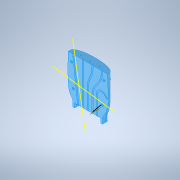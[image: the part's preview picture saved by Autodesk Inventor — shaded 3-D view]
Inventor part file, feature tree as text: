
AUTODESK INVENTOR PART (.ipt)
format: ipt  version: 2021 (Build 250183000, 183)  size: 1,971,200 bytes
history: native  units: mm
features: sketch x38, extrude x24, other x21, fillet x19, plane x11, sweep x4, hole x4, delete_face x1, mirror x1
ambient origin geometry x8: Origin, YZ Plane, XZ Plane, XY Plane, X Axis, Y Axis, Z Axis, Center Point
bodies: Volumenkörper2 (feature_tree), Volumenkörper3 (feature_tree), Volumenkörper4 (feature_tree), Volumenkörper8 (feature_tree), Volumenkörper9 (feature_tree), Volumenkörper10 (feature_tree), Volumenkörper11 (feature_tree), Volumenkörper15 (feature_tree), Volumenkörper16 (feature_tree), Volumenkörper17 (feature_tree), Volumenkörper18 (feature_tree), Volumenkörper19 (feature_tree), Volumenkörper20 (feature_tree), Volumenkörper21 (feature_tree), Volumenkörper24 (feature_tree), Volumenkörper1 (feature_tree)
feature tree (123):
  other  "Form1"
  plane  "Arbeitsebene1"
  extrude  "Extrusion1"  Depth=24.0mm
  fillet  "Rundung1"  Radius=68.0mm
  other  "Kombinieren1"
  fillet  "Rundung2"  Radius=34.0mm
  plane  "Arbeitsebene2"
  extrude  "Extrusion2"  Depth=30.0mm TaperAngle=0.0deg
  other  "Kombinieren2"
  extrude  "Extrusion3"  Depth=15.0mm
  other  "Kombinieren3"
  extrude  "Extrusion4"  Depth=12.0mm
  extrude  "Extrusion10"  Depth=12.0mm
  other  "Kombinieren6"
  plane  "Arbeitsebene3"
  extrude  "Extrusion11"  Depth=9.6mm
  other  "Kombinieren7"
  fillet  "Rundung4"  Radius=9.6mm
  sketch  "Skizze12"  dims[d23=30.0mm d24=45.0mm]
  plane  "Arbeitsebene5"
  extrude  "Daumen Fingerverbindung alt"  Depth=45.0mm
  extrude  "Extrusion30"  Depth=88.7mm TaperAngle=0.0deg
  sketch  "Skizze52"  dims[d209=54.0mm]
  extrude  "Extrusion31"  Depth=30.0mm
  extrude  "Extrusion32"  Depth=60.0mm
  extrude  "Extrusion15"  Depth=2.0mm
  fillet  "Rundung6"  Radius=3.0mm
  fillet  "Rundung19"  Radius=2.0mm
  fillet  "Rundung17"  Radius=7.75mm
  plane  "Arbeitsebene17"
  extrude  "Extrusion33"  Depth=2.0mm
  fillet  "Rundung18"  [1 undecoded]
  other  "Kombinieren8"
  extrude  "Extrusion16"  Depth=111.5mm TaperAngle=0.0deg
  extrude  "Extrusion17"  Depth=8.0mm
  extrude  "Extrusion18"  Depth=5.0mm
  fillet  "Rundung7"  Radius=6.981317mm
  other  "Kombinieren9"
  fillet  "Rundung8"  Radius=9.6mm
  delete_face  "Fläche löschen1"
  fillet  "Rundung10"  Radius=26.0mm
  plane  "Arbeitsebene6"
  plane  "Arbeitsebene7"
  extrude  "Extrusion19"  TaperAngle=0.0deg  [1 undecoded]
  fillet  "Rundung13"  Radius=15.0mm
  sweep  "Sweeping1"
  other  "Kombinieren10"
  fillet  "Rundung11"  Radius=16.0mm
  fillet  "Rundung12"  Radius=60.0mm
  extrude  "Extrusion20"  Depth=12.0mm
  other  "Kombinieren12"
  other  "Kombinieren13"
  plane  "Arbeitsebene11"
  extrude  "Extrusion22"  Depth=1.0mm
  mirror  "Spiegeln2"
  other  "Kombinieren14"
  extrude  "Extrusion23"  Depth=3.4mm
  fillet  "Rundung14"  Radius=30.0mm
  other  "Kombinieren15"
  fillet  "Rundung15"  Radius=5.0mm
  plane  "Arbeitsebene14"
  plane  "Arbeitsebene13"
  sweep  "Sweeping2"
  sweep  "Sweeping3"
  sweep  "Sweeping4"
  extrude  "Extrusion34"  Depth=2.5mm
  other  "Kombinieren17"
  other  "Kombinieren20"
  other  "Kombinieren18"
  other  "Kombinieren19"
  hole  "Bohrung2"  [1 undecoded]
  hole  "Bohrung3"  [1 undecoded]
  plane  "Arbeitsebene16"
  hole  "Bohrung4"  [1 undecoded]
  hole  "Bohrung5"  [1 undecoded]
  fillet  "Rundung20"  Radius=30.0mm
  extrude  "Extrusion37"  Depth=3.0mm
  extrude  "Extrusion36"  Depth=6.0mm
  fillet  "Rundung23"  Radius=10.8mm
  extrude  "Hand_Fingerverbindungen"  [1 undecoded]
  extrude  "Hand_Handhälften"  Depth=32.4mm
  other  "Fingerverbindung_kleinere_Durchmesser"
  other  "Aktivieren bei Handflächenaussenseite"
  fillet  "Rundung Hanflächenaussenseite"  Radius=2.4mm
  other  "Aktivieren bei Handflächeninnenseite"
  fillet  "Rundungi Handflächeninnenseite"  Radius=10.8mm
  sketch  "Skizze1"  dims[d0=-70.0mm d1=24.0mm d2=68.0mm d3=34.0mm]
  sketch  "Skizze2"  dims[d4=16.0mm d5=30.0mm d6=0.0mm]
  sketch  "Skizze3"  dims[d7=5.0mm d8=15.0mm]
  sketch  "Skizze4"  dims[d9=50.0mm d15=12.0mm]
  sketch  "Skizze10"  dims[d16=12.0mm d17=12.0mm]
  sketch  "Skizze11"  dims[d18=9.6mm d19=9.6mm d21=9.6mm]
  sketch  "Skizze14"  dims[d25=45.0mm d27=88.7mm d28=0.0mm]
  sketch  "Skizze17"  dims[d29=45.0mm d31=30.0mm]
  sketch  "Skizze18"  dims[d32=37.2mm d33=60.0mm]
  sketch  "Skizze19"  dims[d34=100.0mm d35=0.0mm d36=9.6mm d37=3.0mm d39=2.0mm d40=7.75mm]
  sketch  "Skizze20"  dims[d41=102.5mm d42=0.0mm d86=2.0mm d87=0.0mm]
  sketch  "Skizze22"  dims[d88=1.0mm d89=111.5mm d90=0.0mm]
  sketch  "Skizze27"  dims[d91=35.0mm d92=8.0mm]
  sketch  "Skizze28"  dims[d93=44.25mm d94=0.0mm d96=5.0mm d97=6.981317mm d99=9.6mm d102=26.0mm]
  sketch  "Skizze29"  dims[d103=90.0deg d104=0.0mm d107=15.0mm]
  sketch  "Skizze31"  dims[d108=25.0mm d109=49.25mm d110=0.0mm d123=16.0mm d124=60.0mm]
  sketch  "Skizze32"  dims[d125=30.0mm d126=12.0mm]
  sketch  "Skizze35"  dims[d127=10.0mm d128=0.0mm d129=1.0mm]
  sketch  "Skizze36"  dims[d130=5.0mm d131=3.4mm d133=30.0mm d134=0.0mm d135=5.0mm]
  sketch  "Skizze37"  dims[d136=3.4mm d138=90.0mm d139=0.0mm]
  sketch  "Skizze38"  dims[d141=17.5mm d142=15.0mm]
  sketch  "Skizze39"  dims[d143=45.0mm d144=90.0mm d145=0.0mm]
  sketch  "Skizze40"  dims[d146=5.0mm d147=2.5mm]
  sketch  "Skizze41"  dims[d149=6.0mm d150=2.0mm]
  sketch  "Skizze42"  dims[d151=6.0mm d161=30.0mm d162=3.0mm]
  sketch  "Skizze44"  dims[d163=6.0mm d164=32.4mm]
  sketch  "Skizze45"  dims[d165=37.5mm d166=0.0mm d183=0.0mm d184=0.0mm d186=30.0mm]
  sketch  "Skizze46"  dims[d187=1.0mm d188=3.0mm]
  sketch  "Skizze47"  dims[d189=3.0mm d190=6.0mm d191=10.8mm]
  sketch  "Skizze50"  dims[d192=70.0mm d193=80.0mm d194=0.0mm d195=0.0mm d204=-1.5mm]
  sketch  "Skizze51"  dims[d205=2.4mm d206=32.4mm d207=2.4mm d208=10.8mm]
  sketch  "Skizze53"  dims[d210=54.0mm]
  sketch  "Skizze54"  dims[d211=13.6mm d212=0.0mm]
  sketch  "Skizze55"  dims[d213=50.0mm]
  sketch  "Skizze57"  dims[d214=9.0mm]
  sketch  "Skizze58"  dims[d215=100.0mm d216=0.0mm d217=2.0mm d218=3.0mm d220=1.745329mm d231=6.0mm d232=92.75mm d233=0.0mm d234=35.0mm d235=116.5mm d236=0.0mm d243=10.0mm d244=3.0mm d245=0.0mm d246=0.0mm d247=21.6mm d248=0.0mm d249=21.6mm d250=0.0mm d251=10.8mm d252=3.0mm d253=0.0mm d254=0.0mm d255=0.0mm d256=0.0mm d257=32.4mm d258=10.8mm d259=30.0mm d260=35.0mm d261=20.0mm d262=35.0mm d263=3.0mm d264=10.8mm d266=0.0mm d267=0.0mm d268=0.0mm d276=0.0mm d277=21.6mm d279=0.5mm d280=3.4mm d281=6.0mm d282=6.5mm d283=4.0mm d284=90.0deg d285=6.0mm d286=0.0mm d287=0.0mm d288=21.6mm d289=0.0mm d290=21.6mm d291=2.4mm d292=6.0mm d293=6.0mm d294=2.0mm d295=90.0deg d296=8.0mm d297=0.0mm d298=0.0mm d299=0.0mm d300=0.0mm d301=0.0mm d302=0.0mm d303=0.0mm d304=0.0mm d305=0.0mm d306=-12.25mm d307=5.5mm d308=6.0mm d309=10.0mm d310=13.8mm d311=90.0deg d312=18.25mm d313=0.0mm d314=18.0mm d315=18.0mm d316=37.0mm d317=37.0mm d318=33.0mm d319=33.0mm d320=33.0mm d321=33.0mm d322=4.2mm d323=6.0mm d324=10.0mm d325=13.8mm d326=90.0deg d327=8.55mm d328=0.0mm d329=0.0mm d330=0.0mm d331=0.0mm d332=0.0mm d333=0.0mm d334=0.0mm d335=0.0mm d336=0.0mm d345=0.5mm d346=16.2mm d349=10.0mm d350=30.0mm d351=0.0mm d354=9.6mm d357=15.0mm d358=0.0mm d359=22.68928mm d360=6.0mm d361=56.3mm d362=6.0mm d363=3.0mm d364=6.0mm d365=7.75mm d366=30.0mm d367=0.0mm d369=-9.5mm d370=2.4mm d371=6.0mm d372=4.8mm d373=30.0mm d374=0.0mm d375=5.0mm d376=3.0mm d377=10.0mm d379=3.0mm d380=2.0mm d381=4.8mm d382=37.0mm d383=0.0mm d384=14.0mm d385=3.0mm d386=1.0mm d399=10.8mm d400=32.4mm d401=1.0mm d402=1.0mm d403=6.0mm d404=6.0mm d405=40.0mm d406=0.0mm d407=2.0mm d415=1.5mm d416=2.0mm d417=4.8mm d418=40.0mm d419=0.0mm d420=2.0mm d66=0.5mm d67=0.872665mm d68=0.5mm d69=0.872665mm d82=0.5mm d83=0.872665mm d84=0.5mm d85=0.872665mm d98=0.872665mm d100=0.872665mm d140=0.5mm d152=0.872665mm d153=0.872665mm d221=0.5mm d222=0.872665mm d223=0.5mm d224=0.872665mm]
  other  "Größe1"
note: 7 required parameter values undecoded (feature->parameter linkage not recoverable at this tier; creation-order binding heuristic only, values carry confidence <= 0.55)
